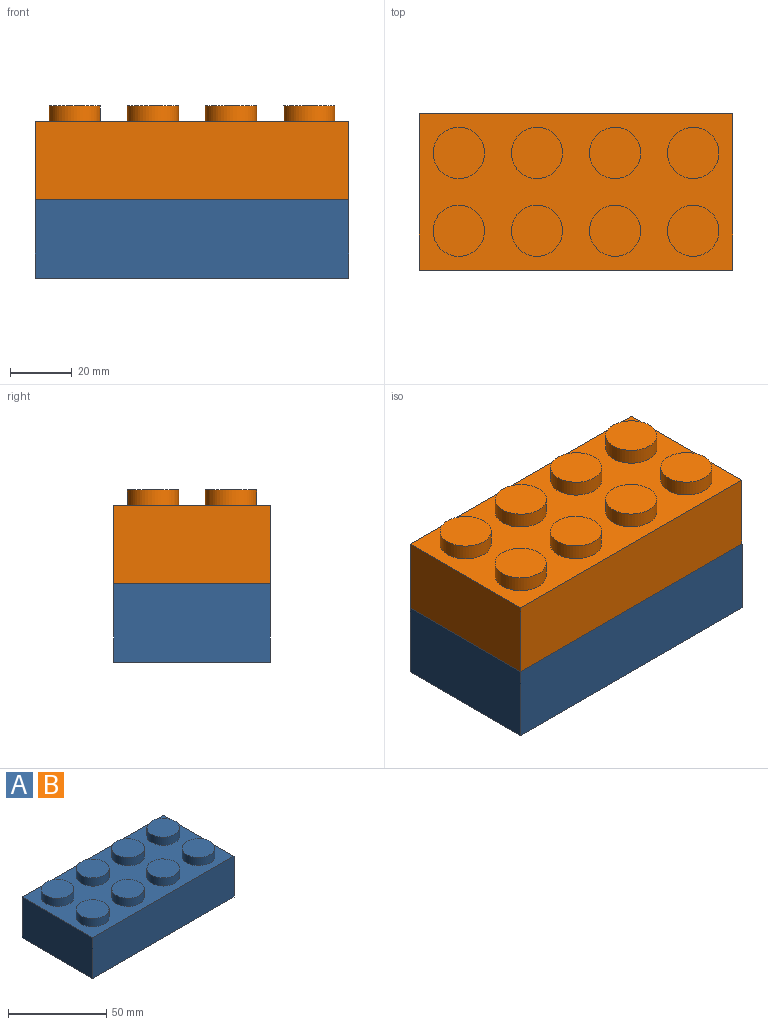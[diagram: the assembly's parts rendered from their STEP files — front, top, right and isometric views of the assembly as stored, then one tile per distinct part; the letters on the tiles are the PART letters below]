
ASSEMBLY  parts=2 mates=1
PART A: 39 faces, bbox 101.6x50.8x30.5 mm
  f0: plane 101.6x25.4mm, normal (0,1,0), area 2580.6mm2, adj f1,f3,f4,f5
  f1: plane 50.8x25.4mm, normal (-1,0,0), area 1290.3mm2, adj f0,f2,f4,f5
  f2: plane 101.6x25.4mm, normal (0,-1,0), area 2580.6mm2, adj f1,f3,f4,f5
  f3: plane 50.8x25.4mm, normal (1,0,0), area 1290.3mm2, adj f0,f2,f4,f5
  f4: plane 101.6x50.8mm, normal (0,0,-1), area 1278.3mm2, adj f0,f1,f2,f3,f22,f23,f24,f27
  f5: plane 101.6x50.8mm, normal (0,0,1), area 3424.3mm2, adj f0,f1,f2,f3,f6,f8,f10,f12
  f6: cylinder r=8.31mm len=16.63mm, axis (0,0,-1), area 265.4mm2, adj f5,f7
  f7: plane 16.63x16.63mm, normal (0,0,1), area 217.1mm2, adj f6
  f8: cylinder r=8.31mm len=16.63mm, axis (0,0,-1), area 265.4mm2, adj f5,f9
  f9: plane 16.63x16.63mm, normal (0,0,1), area 217.1mm2, adj f8
  f10: cylinder r=8.31mm len=16.63mm, axis (0,0,-1), area 265.4mm2, adj f5,f11
  f11: plane 16.63x16.63mm, normal (0,0,1), area 217.1mm2, adj f10
  f12: cylinder r=8.31mm len=16.63mm, axis (0,0,-1), area 265.4mm2, adj f5,f13
  f13: plane 16.63x16.63mm, normal (0,0,1), area 217.1mm2, adj f12
  f14: cylinder r=8.31mm len=16.63mm, axis (0,0,-1), area 265.4mm2, adj f5,f15
  f15: plane 16.63x16.63mm, normal (0,0,1), area 217.1mm2, adj f14
  f16: cylinder r=8.31mm len=16.63mm, axis (0,0,-1), area 265.4mm2, adj f5,f17
  f17: plane 16.63x16.63mm, normal (0,0,1), area 217.1mm2, adj f16
  f18: cylinder r=8.31mm len=16.63mm, axis (0,0,-1), area 265.4mm2, adj f5,f19
  f19: plane 16.63x16.63mm, normal (0,0,1), area 217.1mm2, adj f18
  f20: cylinder r=8.31mm len=16.63mm, axis (0,0,-1), area 265.4mm2, adj f5,f21
  f21: plane 16.63x16.63mm, normal (0,0,1), area 217.1mm2, adj f20
  f22: plane 41.89x22.86mm, normal (1,0,0), area 957.6mm2, adj f4,f23,f27,f29
  f23: plane 92.69x22.86mm, normal (0,-1,0), area 2118.9mm2, adj f4,f22,f24,f29
  f24: plane 41.89x22.86mm, normal (-1,0,0), area 957.6mm2, adj f4,f23,f27,f29
  f25: cylinder r=9.58mm len=22.86mm, axis (0,0,-1), area 1376.5mm2, adj f29,f31
  f26: cylinder r=9.58mm len=22.86mm, axis (0,0,-1), area 1376.5mm2, adj f29,f30
  f27: plane 92.69x22.86mm, normal (0,1,0), area 2118.9mm2, adj f4,f22,f24,f29
  f28: cylinder r=9.58mm len=22.86mm, axis (0,0,-1), area 1376.5mm2, adj f29,f36
  f29: plane 92.69x41.89mm, normal (0,0,-1), area 3017.4mm2, adj f22,f23,f24,f25,f26,f27,f28
  f30: plane 19.17x19.17mm, normal (0,0,-1), area 71.4mm2, adj f26,f34
  f31: plane 19.17x19.17mm, normal (0,0,-1), area 71.4mm2, adj f25,f32
  f32: cylinder r=8.31mm len=22.86mm, axis (0,0,-1), area 1194.1mm2, adj f31,f33
  f33: plane 16.63x16.63mm, normal (0,0,-1), area 217.1mm2, adj f32
  f34: cylinder r=8.31mm len=22.86mm, axis (0,0,-1), area 1194.1mm2, adj f30,f35
  f35: plane 16.63x16.63mm, normal (0,0,-1), area 217.1mm2, adj f34
  f36: plane 19.17x19.17mm, normal (0,0,-1), area 71.4mm2, adj f28,f37
  f37: cylinder r=8.31mm len=22.86mm, axis (0,0,-1), area 1194.1mm2, adj f36,f38
  f38: plane 16.63x16.63mm, normal (0,0,-1), area 217.1mm2, adj f37
PART B: same geometry as A
PLACE A t=(0,0,25.4)mm
PLACE B t=(0,0,50.8)mm
MATE slider A.f26 <-> B.f26  axis (0,0,1) through (0,0,25.4)mm
